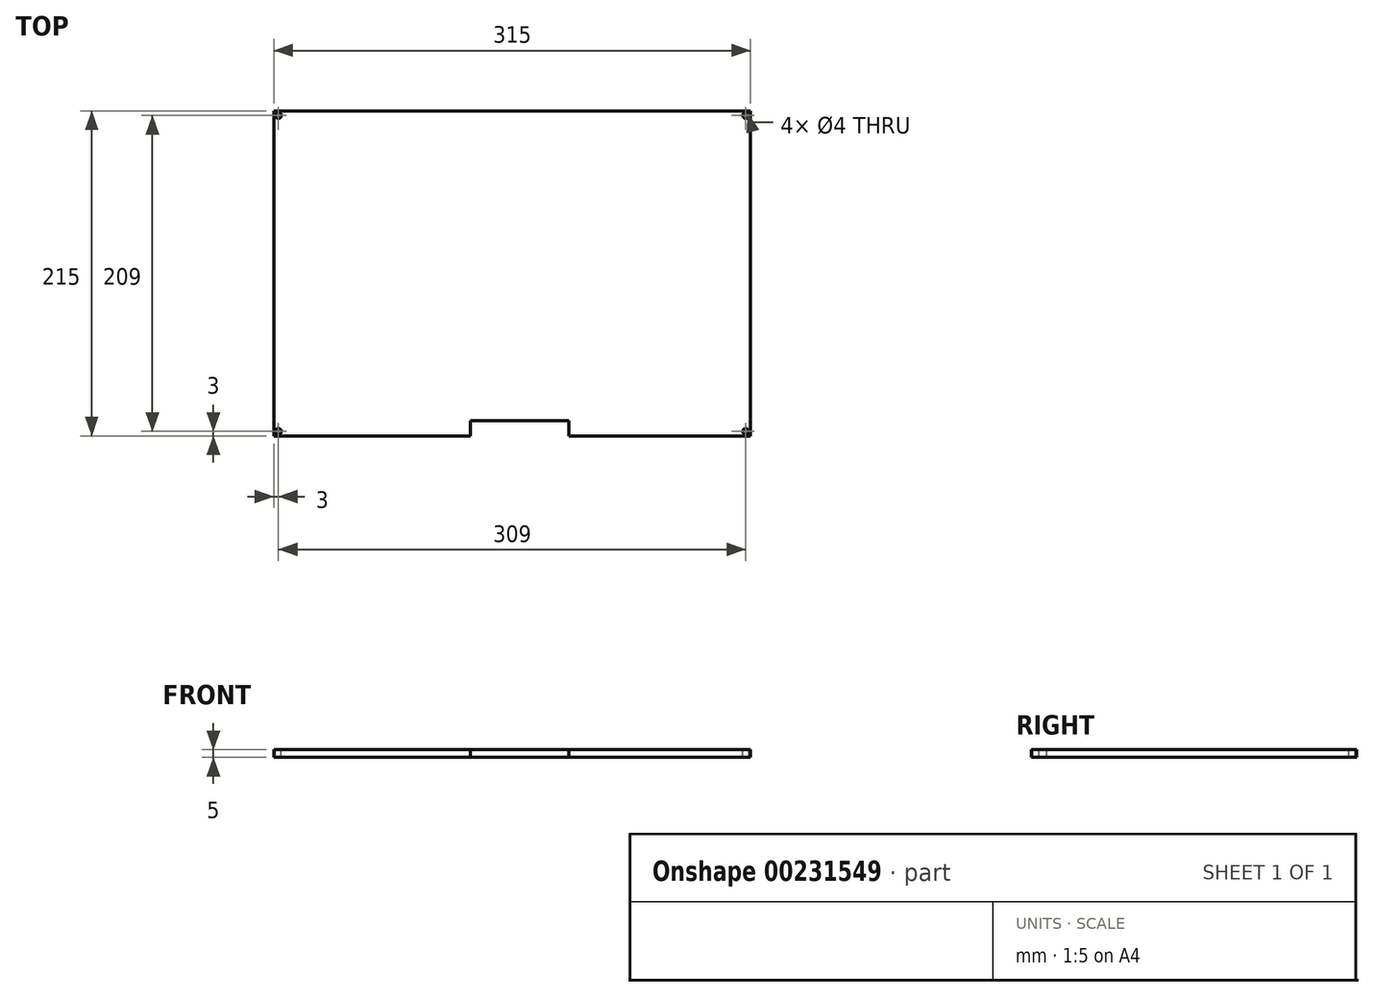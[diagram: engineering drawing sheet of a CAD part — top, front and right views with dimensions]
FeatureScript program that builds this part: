
annotation { "Feature Type Name" : "Feature", "Feature Type Description" : "" }
export const myFeature = defineFeature(function(context is Context, id is Id, definition is map)
    precondition{}
    {
        {
            var Q0;
            Q0=qCreatedBy(makeId("Top.planeOp"),FACE);
            var sketch = newSketch(context, id + "F0", { "sketchPlane" : qUnion([Q0])});
            skLineSegment(sketch, "E0.bottom", {"start": v(-157.5, 107.5) * mm, "end": v(157.5, 107.5) * mm});
            skLineSegment(sketch, "E0.top", {"start": v(-157.5, -107.5) * mm, "end": v(157.5, -107.5) * mm});
            skLineSegment(sketch, "E0.left", {"start": v(-157.5, 107.5) * mm, "end": v(-157.5, -107.5) * mm});
            skLineSegment(sketch, "E0.right", {"start": v(157.5, 107.5) * mm, "end": v(157.5, -107.5) * mm});
            skPoint(sketch, "E0.middle", {"position": v(0, 0) * mm});
            skSolve(sketch);
        }
        {
            var Q0;
            Q0 = qSketchRegion(id + "F0", true);
            extrude(context, id + "F1", {"entities" : qUnion([Q0]), "depth" : 5 * mm});
        }
        {
            var Q0;
            Q0=makeQuery(id+"F1.opExtrude","CAP_FACE",FACE,{"disambiguationData":[OSD([sQuery(id+"F0.wireOp",EDGE,"E0.bottom"),sQuery(id+"F0.wireOp",EDGE,"E0.top"),sQuery(id+"F0.wireOp",EDGE,"E0.left"),sQuery(id+"F0.wireOp",EDGE,"E0.right")])],"isStart":false});
            var sketch = newSketch(context, id + "F2", { "sketchPlane" : qUnion([Q0])});
            skCircle(sketch, "E1", {"center": v(-154.5, -104.5) * mm, "radius": 2 * mm});
            skLineSegment(sketch, "E2", {"start": v(0, 107.5) * mm, "end": v(0, -107.5) * mm, "construction": true});
            skLineSegment(sketch, "E3", {"start": v(-157.5, 0) * mm, "end": v(157.5, 0) * mm, "construction": true});
            skCircle(sketch, "E4.MirrorC", {"center": v(154.5, -104.5) * mm, "radius": 2 * mm});
            skCircle(sketch, "E5.MirrorC", {"center": v(154.5, 104.5) * mm, "radius": 2 * mm});
            skCircle(sketch, "E6.MirrorC", {"center": v(-154.5, 104.5) * mm, "radius": 2 * mm});
            skLineSegment(sketch, "E7", {"start": v(-27.5, -107.5) * mm, "end": v(-27.5, -97.5) * mm});
            skLineSegment(sketch, "E8", {"start": v(-27.5, -97.5) * mm, "end": v(37.5, -97.5) * mm});
            skLineSegment(sketch, "E9", {"start": v(37.5, -97.5) * mm, "end": v(37.5, -107.5) * mm});
            skLineSegment(sketch, "E10.0", {"start": v(-157.5, -107.5) * mm, "end": v(157.5, -107.5) * mm});
            skSolve(sketch);
        }
        {
            var Q0;
            Q0 = qSketchRegion(id + "F2", true);
            extrude(context, id + "F3", {"entities" : qUnion([Q0]), "operationType" : NewBodyOperationType.REMOVE, "endBound" : BoundingType.THROUGH_ALL, "oppositeDirection" : true, "depth" : 25 * mm});
        }
    });
